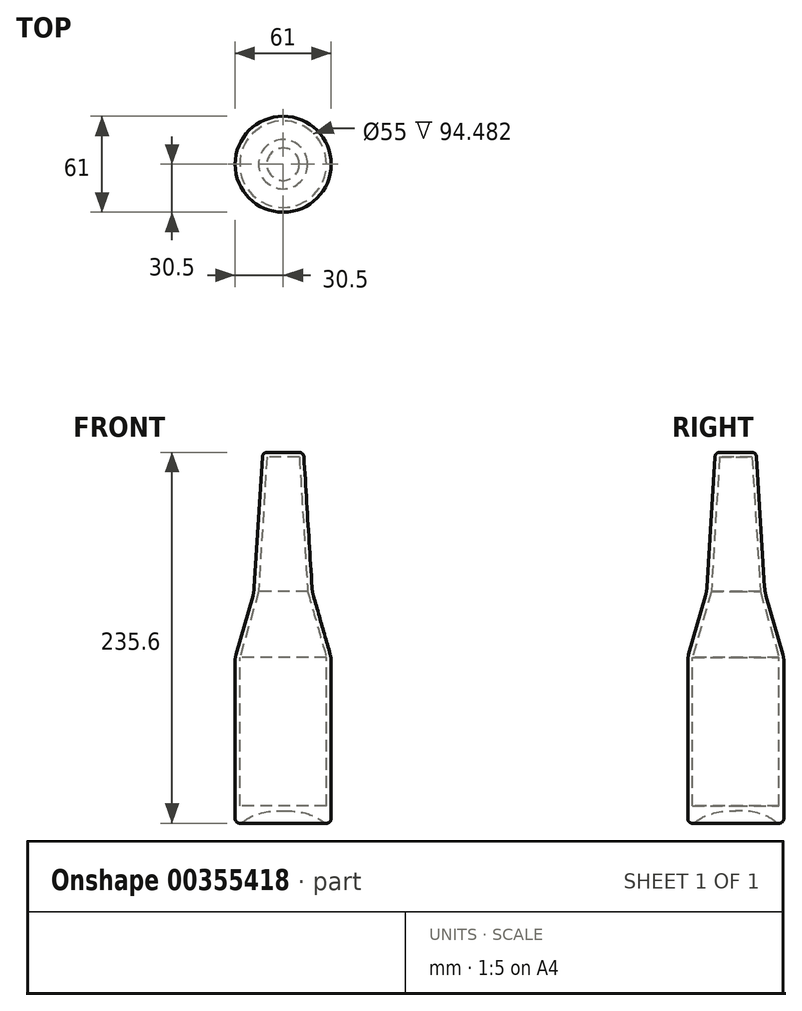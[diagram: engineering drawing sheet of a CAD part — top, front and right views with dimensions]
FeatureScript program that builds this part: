
annotation { "Feature Type Name" : "Feature", "Feature Type Description" : "" }
export const myFeature = defineFeature(function(context is Context, id is Id, definition is map)
    precondition{}
    {
        {
            var Q0;
            Q0=qCreatedBy(makeId("Front.planeOp"),FACE);
            var sketch = newSketch(context, id + "F0", { "sketchPlane" : qUnion([Q0])});
            skLineSegment(sketch, "E0", {"start": v(0, 120.73) * mm, "end": v(0, -179.96) * mm, "construction": true});
            skLineSegment(sketch, "E1", {"start": v(30.5, -144.1) * mm, "end": v(30.5, -44.1) * mm});
            skLineSegment(sketch, "E2", {"start": v(29.92, -39.98) * mm, "end": v(19.25, -2.6) * mm});
            skLineSegment(sketch, "E3", {"start": v(18.33, 2.7) * mm, "end": v(13.17, 85.69) * mm});
            skLineSegment(sketch, "E4", {"start": v(10.18, 88.5) * mm, "end": v(0, 88.5) * mm});
            skFitSpline(sketch, "E5", {"points": [v(0, -139.1) * mm, v(16.61, -141.42) * mm, v(30.5, -153) * mm], "startDerivative": vector(33.91, 0) * mm, "endDerivative": vector(17.67, -37.48) * mm});
            skArc(sketch, "E6.filletArc", {"start": v(25.52, -146.35) * mm, "mid": v(28.74, -146.83) * mm, "end": v(30.5, -144.1) * mm});
            skPoint(sketch, "E7.visualSharp", {"position": v(13, 88.5) * mm});
            skArc(sketch, "E7.filletArc", {"start": v(13.17, 85.69) * mm, "mid": v(12.24, 87.69) * mm, "end": v(10.18, 88.5) * mm});
            skPoint(sketch, "E8.visualSharp", {"position": v(18.5, 0) * mm});
            skArc(sketch, "E8.filletArc", {"start": v(18.33, 2.7) * mm, "mid": v(18.64, 0.02) * mm, "end": v(19.25, -2.6) * mm});
            skPoint(sketch, "E9.visualSharp", {"position": v(30.5, -42) * mm});
            skArc(sketch, "E9.filletArc", {"start": v(30.5, -44.1) * mm, "mid": v(30.36, -42.02) * mm, "end": v(29.92, -39.98) * mm});
            skLineSegment(sketch, "E10", {"start": v(0, 88.5) * mm, "end": v(0, 85.5) * mm});
            skLineSegment(sketch, "E11", {"start": v(0, 85.5) * mm, "end": v(10.3, 85.5) * mm});
            skLineSegment(sketch, "E12", {"start": v(10.3, 85.5) * mm, "end": v(15.6, 0) * mm});
            skLineSegment(sketch, "E13", {"start": v(15.6, 0) * mm, "end": v(27.5, -41.62) * mm});
            skLineSegment(sketch, "E14", {"start": v(27.5, -41.62) * mm, "end": v(27.5, -136.1) * mm});
            skLineSegment(sketch, "E15", {"start": v(27.5, -136.1) * mm, "end": v(0, -136.1) * mm});
            skLineSegment(sketch, "E16", {"start": v(0, -136.1) * mm, "end": v(0, -139.1) * mm});
            skSolve(sketch);
        }
        {
            var Q0;
            Q0=qSketchRegion(id+"F0",true);
            var Q1;
            Q1=sQuery(id+"F0.wireOp",EDGE,"E0");
            revolve(context, id + "F1", {"entities" : qUnion([Q0]), "axis" : qUnion([Q1]), "revolveType" : RevolveType.FULL});
        }
    });
